FCSTD DOCUMENT  (FreeCAD 0.22R37100 (Git))
Label: composit_stand8_model
License: All rights reserved
LicenseURL: http://en.wikipedia.org/wiki/All_rights_reserved
objects: App::Link×25, App::DocumentObjectGroup×4, Part::FeaturePython×2, PartDesign::CoordinateSystem×1, App::FeaturePython×1, PartDesign::Plane×1, App::AnnotationLabel×1, App::Part×1
note: 4 computed .brp shape members not serialized (recipe doc carries the construction recipe); baked Part::Feature solids carry a one-line shape summary decoded from their .brp
EXTERNAL_REF file=composit_stand8.FCStd obj=Local_CS005
EXTERNAL_REF file=composit_stand8.FCStd obj=Body
EXTERNAL_REF file=composit_stand8.FCStd obj=Local_CS004
EXTERNAL_REF file=composit_stand8.FCStd obj=Local_CS006
EXTERNAL_REF file=composit_stand8.FCStd obj=Body003
EXTERNAL_REF file=composit_stand8.FCStd obj=Local_CS007
EXTERNAL_REF file=composit_stand8.FCStd obj=Local_CS008
EXTERNAL_REF file=composit_stand8.FCStd obj=Local_CS010
EXTERNAL_REF file=composit_stand8.FCStd obj=Body002
EXTERNAL_REF file=composit_stand8.FCStd obj=Local_CS011
EXTERNAL_REF file=composit_stand8.FCStd obj=Local_CS012
EXTERNAL_REF file=composit_stand8.FCStd obj=Local_CS013
EXTERNAL_REF file=composit_stand8.FCStd obj=Body004
EXTERNAL_REF file=composit_stand8.FCStd obj=Local_CS015
EXTERNAL_REF file=composit_stand8.FCStd obj=Local_CS016
EXTERNAL_REF file=composit_stand8.FCStd obj=Body005
EXTERNAL_REF file=composit_stand8.FCStd obj=Local_CS017
EXTERNAL_REF file=composit_stand8.FCStd obj=Body006
EXTERNAL_REF file=composit_stand8.FCStd obj=Local_CS014
EXTERNAL_REF file=composit_stand8.FCStd obj=Local_CS018
EXTERNAL_REF file=composit_stand8.FCStd obj=Local_CS019
EXTERNAL_REF file=composit_stand8.FCStd obj=Part
EXTERNAL_REF file=composit_stand8.FCStd obj=Local_CS020
EXTERNAL_REF file=composit_stand8.FCStd obj=Body007
EXTERNAL_REF file=composit_stand8.FCStd obj=Local_CS025
EXTERNAL_REF file=composit_stand8.FCStd obj=Local_CS026
EXTERNAL_REF file=composit_stand8.FCStd obj=Body012
EXTERNAL_REF file=composit_stand8.FCStd obj=Local_CS027
EXTERNAL_REF file=composit_stand8.FCStd obj=Body013
EXTERNAL_REF file=ULZ-P02-14W.FCStd obj=Local_CS
EXTERNAL_REF file=composit_stand8.FCStd obj=Local_CS028
EXTERNAL_REF file=ULZ-P02-14W.FCStd obj=Body
EXTERNAL_REF file=composit_stand8.FCStd obj=Local_CS030
EXTERNAL_REF file=composit_stand8.FCStd obj=Local_CS032
EXTERNAL_REF file=composit_stand8.FCStd obj=Body018
EXTERNAL_REF file=composit_stand8.FCStd obj=Local_CS031
EXTERNAL_REF file=composit_stand8.FCStd obj=Body019
EXTERNAL_REF file=composit_stand8.FCStd obj=Local_CS033
EXTERNAL_REF file=composit_stand8.FCStd obj=Body017
EXTERNAL_REF file=composit_electric_shield.FCStd obj=Local_CS
EXTERNAL_REF file=composit_stand8.FCStd obj=Local_CS034
EXTERNAL_REF file=composit_electric_shield.FCStd obj=Body
EXTERNAL_REF file=composit_stand8.FCStd obj=Local_CS037
EXTERNAL_REF file=composit_stand8.FCStd obj=Body026
EXTERNAL_REF file=composit_stand8.FCStd obj=Local_CS038
EXTERNAL_REF file=composit_stand8.FCStd obj=Local_CS039
EXTERNAL_REF file=composit_stand8.FCStd obj=Body027
EXTERNAL_REF file=composit_stand8.FCStd obj=Local_CS040
EXTERNAL_REF file=composit_stand8.FCStd obj=Local_CS041
EXTERNAL_REF file=composit_stand8.FCStd obj=Body030

FEATURE [App::DocumentObjectGroup] Parts
FEATURE [PartDesign::CoordinateSystem] LCS_Origin
  AttacherType = Attacher::AttachEngine3D
  AttachmentSupport = -> [XY_Plane]
  MapMode = 2
FEATURE [App::DocumentObjectGroup] Constraints
FEATURE [App::FeaturePython] Variables  # WARN: FeaturePython — macro-defined, semantics opaque (R4)
  Type = App::PropertyContainer
FEATURE [App::DocumentObjectGroup] Configurations
FEATURE [App::Link] face
  AttachedBy = #Local_CS005
  AttachedTo = Parent Assembly#LCS_Origin
  AttachmentOffset = pos=(0,0,0) rot=(0,0,1;3.14159rad)
  LinkPlacement = pos=(0,0,0) rot=(0,0,1;3.14159rad)
  LinkedObject = -> <external composit_stand8.FCStd>#Body
  Placement = pos=(0,0,0) rot=(0,0,1;3.14159rad)
  SolverId = Asm4EE
  expr: Placement = LCS_Origin.Placement * AttachmentOffset * composit_stand8#Local_CS005.Placement ^ -1
FEATURE [App::Link] sink
  AttachedBy = #Local_CS004
  AttachedTo = face#Local_CS006
  LinkPlacement = pos=(-319.563,-20,100) rot=(0,0,1;3.14159rad)
  LinkedObject = -> <external composit_stand8.FCStd>#Body003
  Placement = pos=(-319.563,-20,100) rot=(0,0,1;3.14159rad)
  SolverId = Asm4EE
  expr: Placement = face.Placement * composit_stand8#Local_CS006.Placement * AttachmentOffset * composit_stand8#Local_CS004.Placement ^ -1
FEATURE [App::Link] sink001
  AttachedBy = #Local_CS004
  AttachedTo = face#Local_CS007
  LinkPlacement = pos=(319.563,-20,100) rot=(0,0,1;3.14159rad)
  LinkedObject = -> <external composit_stand8.FCStd>#Body003
  Placement = pos=(319.563,-20,100) rot=(0,0,1;3.14159rad)
  SolverId = Asm4EE
  expr: Placement = face.Placement * composit_stand8#Local_CS007.Placement * AttachmentOffset * composit_stand8#Local_CS004.Placement ^ -1
FEATURE [App::Link] dropper_fix_composit
  AttachedBy = #Local_CS008
  AttachedTo = face#Local_CS010
  AttachmentOffset = pos=(0,0,0.4) rot=(0,0,1;0rad)
  LinkPlacement = pos=(-319.563,3.91e-14,1100.4) rot=(0,0,1;3.14159rad)
  LinkedObject = -> <external composit_stand8.FCStd>#Body002
  Placement = pos=(-319.563,3.91e-14,1100.4) rot=(0,0,1;3.14159rad)
  SolverId = Asm4EE
  expr: Placement = face.Placement * composit_stand8#Local_CS010.Placement * AttachmentOffset * composit_stand8#Local_CS008.Placement ^ -1
FEATURE [App::Link] dropper_fix_composit001
  AttachedBy = #Local_CS008
  AttachedTo = face#Local_CS011
  AttachmentOffset = pos=(0,0,0.4) rot=(0,0,1;0rad)
  LinkPlacement = pos=(319.563,-3.91e-14,1100.4) rot=(0,0,1;3.14159rad)
  LinkedObject = -> <external composit_stand8.FCStd>#Body002
  Placement = pos=(319.563,-3.91e-14,1100.4) rot=(0,0,1;3.14159rad)
  SolverId = Asm4EE
  expr: Placement = face.Placement * composit_stand8#Local_CS011.Placement * AttachmentOffset * composit_stand8#Local_CS008.Placement ^ -1
FEATURE [App::Link] dropper_fix_PP
  AttachedBy = #Local_CS012
  AttachedTo = dropper_fix_composit#Local_CS013
  LinkPlacement = pos=(-319.563,3.91e-14,1103.4) rot=(0,0,1;3.14159rad)
  LinkedObject = -> <external composit_stand8.FCStd>#Body004
  Placement = pos=(-319.563,3.91e-14,1103.4) rot=(0,0,1;3.14159rad)
  SolverId = Asm4EE
  expr: Placement = dropper_fix_composit.Placement * composit_stand8#Local_CS013.Placement * AttachmentOffset * composit_stand8#Local_CS012.Placement ^ -1
FEATURE [App::Link] dropper_fix_PP001
  AttachedBy = #Local_CS012
  AttachedTo = dropper_fix_composit001#Local_CS013
  LinkPlacement = pos=(319.563,-3.91e-14,1103.4) rot=(0,0,1;3.14159rad)
  LinkedObject = -> <external composit_stand8.FCStd>#Body004
  Placement = pos=(319.563,-3.91e-14,1103.4) rot=(0,0,1;3.14159rad)
  SolverId = Asm4EE
  expr: Placement = dropper_fix_composit001.Placement * composit_stand8#Local_CS013.Placement * AttachmentOffset * composit_stand8#Local_CS012.Placement ^ -1
FEATURE [App::Link] bar001
  AttachedBy = #Local_CS016
  AttachedTo = face#Local_CS015
  LinkPlacement = pos=(636.126,-17,883.5) rot=(0,1,0;4.71239rad)
  LinkedObject = -> <external composit_stand8.FCStd>#Body005
  Placement = pos=(636.126,-17,883.5) rot=(0,1,0;4.71239rad)
  SolverId = Asm4EE
  expr: Placement = face.Placement * composit_stand8#Local_CS015.Placement * AttachmentOffset * composit_stand8#Local_CS016.Placement ^ -1
FEATURE [App::Link] bar_fix001
  AttachedBy = #Local_CS017
  AttachedTo = bar001#Local_CS016
  AttachmentOffset = pos=(0,16,0) rot=(0,0,1;0rad)
  LinkPlacement = pos=(636.126,-1,883.5) rot=(-0.707107,0,0.707107;3.14159rad)
  LinkedObject = -> <external composit_stand8.FCStd>#Body006
  Placement = pos=(636.126,-1,883.5) rot=(-0.707107,0,0.707107;3.14159rad)
  SolverId = Asm4EE
  expr: Placement = bar001.Placement * composit_stand8#Local_CS016.Placement * AttachmentOffset * composit_stand8#Local_CS017.Placement ^ -1
FEATURE [App::Link] bar002
  AttachedBy = #Local_CS016
  AttachedTo = face#Local_CS014
  LinkPlacement = pos=(636.126,-17,220) rot=(0,1,0;4.71239rad)
  LinkedObject = -> <external composit_stand8.FCStd>#Body005
  Placement = pos=(636.126,-17,220) rot=(0,1,0;4.71239rad)
  SolverId = Asm4EE
  expr: Placement = face.Placement * composit_stand8#Local_CS014.Placement * AttachmentOffset * composit_stand8#Local_CS016.Placement ^ -1
FEATURE [App::Link] bar_fix
  AttachedBy = #Local_CS017
  AttachedTo = bar002#Local_CS016
  LinkPlacement = pos=(636.126,-17,220) rot=(-0.707107,0,0.707107;3.14159rad)
  LinkedObject = -> <external composit_stand8.FCStd>#Body006
  Placement = pos=(636.126,-17,220) rot=(-0.707107,0,0.707107;3.14159rad)
  SolverId = Asm4EE
  expr: Placement = bar002.Placement * composit_stand8#Local_CS016.Placement * AttachmentOffset * composit_stand8#Local_CS017.Placement ^ -1
FEATURE [App::Link] bar_fix002
  AttachedBy = #Local_CS017
  AttachedTo = bar001#Local_CS018
  LinkPlacement = pos=(-636.126,-17,883.5) rot=(-0.707107,0,-0.707107;3.14159rad)
  LinkedObject = -> <external composit_stand8.FCStd>#Body006
  Placement = pos=(-636.126,-17,883.5) rot=(-0.707107,0,-0.707107;3.14159rad)
  SolverId = Asm4EE
  expr: Placement = bar001.Placement * composit_stand8#Local_CS018.Placement * AttachmentOffset * composit_stand8#Local_CS017.Placement ^ -1
FEATURE [App::Link] bar_fix003
  AttachedBy = #Local_CS017
  AttachedTo = bar002#Local_CS018
  LinkPlacement = pos=(-636.126,-17,220) rot=(-0.707107,0,-0.707107;3.14159rad)
  LinkedObject = -> <external composit_stand8.FCStd>#Body006
  Placement = pos=(-636.126,-17,220) rot=(-0.707107,0,-0.707107;3.14159rad)
  SolverId = Asm4EE
  expr: Placement = bar002.Placement * composit_stand8#Local_CS018.Placement * AttachmentOffset * composit_stand8#Local_CS017.Placement ^ -1
FEATURE [App::Link] modules
  AttachedBy = #Local_CS019
  AttachedTo = face#Local_CS005
  LinkPlacement = pos=(0,0,0) rot=(0,0,1;3.14159rad)
  LinkedObject = -> <external composit_stand8.FCStd>#Part
  Placement = pos=(0,0,0) rot=(0,0,1;3.14159rad)
  SolverId = Asm4EE
  expr: Placement = face.Placement * composit_stand8#Local_CS005.Placement * AttachmentOffset * composit_stand8#Local_CS019.Placement ^ -1
FEATURE [App::Link] sink_back
  AttachedBy = #Local_CS020
  AttachedTo = sink#Local_CS004
  LinkPlacement = pos=(-319.563,-17,100) rot=(0,0,1;3.14159rad)
  LinkedObject = -> <external composit_stand8.FCStd>#Body007
  Placement = pos=(-319.563,-17,100) rot=(0,0,1;3.14159rad)
  SolverId = Asm4EE
  expr: Placement = sink.Placement * composit_stand8#Local_CS004.Placement * AttachmentOffset * composit_stand8#Local_CS020.Placement ^ -1
FEATURE [PartDesign::Plane] Plane_1
  Length = 100
  MapMode = 4
  Placement = pos=(0,0,0) rot=(0.57735,0.57735,0.57735;2.0944rad)
  ResizeMode = 1
  Width = 100
FEATURE [Part::FeaturePython] Mirror_sink_back  # Draft array (typed FeaturePython)
  ArrayType = Mirror Array
  Axis = -> Plane_1
  AxisPlacement = pos=(0,0,0) rot=(0.57735,0.57735,0.57735;2.0944rad)
  Count = 2
  Index = 1
  PlacementList = 2 placements: [(-319.563,-17,100),(319.563,-17,100)]
  Placer = pos=(-34,200,639.126) rot=(0,0,1;3.14159rad)
  ScaleList = (2) [(1,1,1),(-1,-1,-1)]
  Scaler = -1
  ShowElement = false
  SourceObject = -> sink_back
  expr: .Placer.Base = .Placer.Rotation * minvert(.AxisPlacement) * .SourceObject.Placement.Base * -2 * (Index % 2)
  expr: .Placer.Rotation.Angle = 180 * (Index % 2)
  expr: Scaler = 1 - 2 * (Index % 2)
FEATURE [App::Link] lamp_fix
  AttachedBy = #Local_CS026
  AttachedTo = face#Local_CS025
  LinkPlacement = pos=(-319.563,3.91e-14,182) rot=(0,0,1;3.14159rad)
  LinkedObject = -> <external composit_stand8.FCStd>#Body012
  Placement = pos=(-319.563,3.91e-14,182) rot=(0,0,1;3.14159rad)
  SolverId = Asm4EE
  expr: Placement = face.Placement * composit_stand8#Local_CS025.Placement * AttachmentOffset * composit_stand8#Local_CS026.Placement ^ -1
FEATURE [App::Link] lamp_fix_mirror
  AttachedBy = #Local_CS027
  AttachedTo = face#Local_CS025
  LinkPlacement = pos=(-319.563,3.91e-14,182) rot=(0,0,1;3.14159rad)
  LinkedObject = -> <external composit_stand8.FCStd>#Body013
  Placement = pos=(-319.563,3.91e-14,182) rot=(0,0,1;3.14159rad)
  SolverId = Asm4EE
  expr: Placement = face.Placement * composit_stand8#Local_CS025.Placement * AttachmentOffset * composit_stand8#Local_CS027.Placement ^ -1
FEATURE [App::Link] Body
  AttachedBy = #Local_CS
  AttachedTo = lamp_fix#Local_CS028
  LinkPlacement = pos=(-600.201,-195.271,632) rot=(0.313146,0.671543,0.671543;2.53465rad)
  LinkedObject = -> <external ULZ-P02-14W.FCStd>#Body
  Placement = pos=(-600.201,-195.271,632) rot=(0.313146,0.671543,0.671543;2.53465rad)
  SolverId = Asm4EE
  expr: Placement = lamp_fix.Placement * composit_stand8#Local_CS028.Placement * AttachmentOffset * ULZ_P02_14W#Local_CS.Placement ^ -1
FEATURE [App::Link] cap_outer
  AttachedBy = #Local_CS030
  AttachedTo = face#Local_CS032
  LinkPlacement = pos=(0,0,1100) rot=(0,0,1;3.14159rad)
  LinkedObject = -> <external composit_stand8.FCStd>#Body018
  Placement = pos=(0,0,1100) rot=(0,0,1;3.14159rad)
  SolverId = Asm4EE
  expr: Placement = face.Placement * composit_stand8#Local_CS032.Placement * AttachmentOffset * composit_stand8#Local_CS030.Placement ^ -1
FEATURE [App::Link] cap_inner
  AttachedBy = #Local_CS031
  AttachedTo = cap_outer#Local_CS030
  LinkPlacement = pos=(0,0,1100) rot=(0,0,1;3.14159rad)
  LinkedObject = -> <external composit_stand8.FCStd>#Body019
  Placement = pos=(0,0,1100) rot=(0,0,1;3.14159rad)
  SolverId = Asm4EE
  expr: Placement = cap_outer.Placement * composit_stand8#Local_CS030.Placement * AttachmentOffset * composit_stand8#Local_CS031.Placement ^ -1
FEATURE [App::Link] drain_holder
  AttachedBy = #Local_CS033
  AttachedTo = face#Local_CS005
  LinkPlacement = pos=(0,0,0) rot=(0,0,1;3.14159rad)
  LinkedObject = -> <external composit_stand8.FCStd>#Body017
  Placement = pos=(0,0,0) rot=(0,0,1;3.14159rad)
  SolverId = Asm4EE
  expr: Placement = face.Placement * composit_stand8#Local_CS005.Placement * AttachmentOffset * composit_stand8#Local_CS033.Placement ^ -1
FEATURE [Part::FeaturePython] DistPoints  # WARN: FeaturePython — macro-defined, semantics opaque (R4)
FEATURE [App::AnnotationLabel] MeasureLbl
  BasePosition = (10,-87.9055,26.7108)
  LabelText = D = 34,1891 mm
  TextPosition = (0,0,0)
FEATURE [App::DocumentObjectGroup] Measures
  Group = -> [DistPoints,MeasureLbl]
FEATURE [App::Link] composit_electric_shield_inner
  AttachedBy = #Local_CS
  AttachedTo = face#Local_CS034
  LinkPlacement = pos=(605.726,-60,610) rot=(0.57735,0.57735,0.57735;2.0944rad)
  LinkedObject = -> <external composit_electric_shield.FCStd>#Body
  Placement = pos=(605.726,-60,610) rot=(0.57735,0.57735,0.57735;2.0944rad)
  SolverId = Asm4EE
  expr: Placement = face.Placement * composit_stand8#Local_CS034.Placement * AttachmentOffset * composit_electric_shield#Local_CS.Placement ^ -1
FEATURE [App::Link] basin_shield_wall
  AttachedBy = #Local_CS037
  AttachedTo = face#Local_CS005
  AttachmentOffset = pos=(0,0,-500) rot=(0,0,1;0rad)
  LinkPlacement = pos=(0,0,-500) rot=(0,0,1;3.14159rad)
  LinkedObject = -> <external composit_stand8.FCStd>#Body026
  Placement = pos=(0,0,-500) rot=(0,0,1;3.14159rad)
  SolverId = Asm4EE
  expr: Placement = face.Placement * composit_stand8#Local_CS005.Placement * AttachmentOffset * composit_stand8#Local_CS037.Placement ^ -1
FEATURE [App::Link] basin_shield_top
  AttachedBy = #Local_CS039
  AttachedTo = basin_shield_wall#Local_CS038
  LinkPlacement = pos=(0,0,-252) rot=(0,0,1;3.14159rad)
  LinkedObject = -> <external composit_stand8.FCStd>#Body027
  Placement = pos=(0,0,-252) rot=(0,0,1;3.14159rad)
  SolverId = Asm4EE
  expr: Placement = basin_shield_wall.Placement * composit_stand8#Local_CS038.Placement * AttachmentOffset * composit_stand8#Local_CS039.Placement ^ -1
FEATURE [App::Link] basin_shield_corrugation
  AttachedBy = #Local_CS041
  AttachedTo = basin_shield_top#Local_CS040
  LinkPlacement = pos=(0,0,-252) rot=(0,0,1;3.14159rad)
  LinkedObject = -> <external composit_stand8.FCStd>#Body030
  Placement = pos=(0,0,-252) rot=(0,0,1;3.14159rad)
  SolverId = Asm4EE
  expr: Placement = basin_shield_top.Placement * composit_stand8#Local_CS040.Placement * AttachmentOffset * composit_stand8#Local_CS041.Placement ^ -1
FEATURE [App::Part] Assembly
  AssemblyType = Part::Link
  Group = -> [LCS_Origin,Constraints,Variables,Configurations,face,sink,sink001,dropper_fix_composit,dropper_fix_composit001,dropper_fix_PP,dropper_fix_PP001,bar001,bar_fix001,bar002,bar_fix,bar_fix002,bar_fix003,modules,sink_back,Plane_1,Mirror_sink_back,lamp_fix,lamp_fix_mirror,Body,cap_outer,cap_inner,drain_holder,composit_electric_shield_inner,basin_shield_wall,basin_shield_top,basin_shield_corrugation]
  Origin = -> Origin
  Type = Assembly

RESOLVED EXTERNAL PARTS (link-assembly join: the EXTERNAL_REF files above that resolve inside this repo's crawl, each included once):
---- part ULZ-P02-14W.FCStd = doc fcstd_d946428e1785 ----
FCSTD DOCUMENT  (FreeCAD 1.1R38827 (Git))
Label: ULZ-P02-14W
License: All rights reserved
LicenseURL: http://en.wikipedia.org/wiki/All_rights_reserved
objects: Sketcher::SketchObject×4, Part::FeaturePython×4, App::DocumentObjectGroup×3, Path::FeaturePython×3, App::FeaturePython×1, Part::Part2DObjectPython×1, PartDesign::SubShapeBinder×1, PartDesign::Pad×1, PartDesign::CoordinateSystem×1, PartDesign::Body×1
note: 20 computed .brp shape members not serialized (recipe doc carries the construction recipe); baked Part::Feature solids carry a one-line shape summary decoded from their .brp

FEATURE [Sketcher::SketchObject] Sketch  label="holes"
  ArcFitTolerance = 0
  FullyConstrained = true
  MakeInternals = false
  sketch-geometry (3):
    g0: Circle CenterX=-4.15 CenterY=445 CenterZ=0 NormalX=0 NormalY=0 NormalZ=1 AngleXU=0 Radius=1.6
    g1: Circle CenterX=4.15 CenterY=-445 CenterZ=0 NormalX=0 NormalY=0 NormalZ=1 AngleXU=0 Radius=1.6
    g2: GeomPoint [constr] X=-9.05 Y=0 Z=0
  constraints (8):
    c: Symmetric(g1,g0,g-1)
    c: Distance(g0,g1) = 890.039
    c: PointOnObject(g2,g-1)
    c: DistanceX(g2,g0) = 4.9
    c: DistanceX(g2) = -9.05
    c: DistanceY(g1,g0) = 890
    c: Equal(g1,g0)
    c: Diameter(g1) = 3.2
FEATURE [App::FeaturePython] SetupSheet  # Path/CAM operation (typed FeaturePython)
  ClearanceHeightExpression = OpStockZMax+SetupSheet.ClearanceHeightOffset
  ClearanceHeightOffset = 5
  CoolantMode = 0
  CoolantModes = None | Flood | Mist
  FinalDepthExpression = -0.1 mm
  HorizRapid = 0
  ProfileDirection = 1
  ProfileSide = 0
  ProfileUseComp = true
  ProfileprocessCircles = true
  ProfileprocessHoles = true
  ProfileprocessPerimeter = true
  SafeHeightExpression = OpStockZMax+SetupSheet.SafeHeightOffset
  SafeHeightOffset = 3
  StartDepthExpression = 3 mm
  StepDownExpression = 4 mm
  VertRapid = 0
FEATURE [Part::Part2DObjectPython] Clone2D  label="Model-Sketch"  # Draft 2D object (typed FeaturePython)
  Fuse = false
  Objects = -> [Sketch]
  PathResource = Model
  Placement = pos=(-5.75,446.581,0) rot=(0,0,1;0rad)
  Scale = (1,1,1)
FEATURE [App::DocumentObjectGroup] Model
  Group = -> [Clone2D]
FEATURE [Part::FeaturePython] ToolBit  label="3.175mm Endmill"  # Path/CAM toolbit (typed FeaturePython)
  BitPropertyNames = Chipload | CuttingEdgeHeight | Diameter | Flutes | Length | Material | ShankDiameter | SpindleDirection
  BitShape = <path>
  Chipload = 0
  CuttingEdgeHeight = 30
  Diameter = 3.175
  Flutes = 0
  Length = 10
  Material = 0
  ShankDiameter = 3
  ShapeName = endmill
  SpindleDirection = 0
FEATURE [Path::FeaturePython] __175mm_Endmill  label="3.175mm Endmill001"  # Path/CAM operation (typed FeaturePython)
  HorizFeed = 33.3333
  HorizRapid = 0
  SpindleDir = 0
  SpindleSpeed = 18000
  Tool = -> ToolBit
  ToolNumber = 1
  VertFeed = 8.33333
  VertRapid = 0
  expr: HorizRapid = SetupSheet.HorizRapid
  expr: VertRapid = SetupSheet.VertRapid
FEATURE [App::DocumentObjectGroup] Tools
  Group = -> [__175mm_Endmill]
FEATURE [Part::FeaturePython] Stock  # WARN: FeaturePython — macro-defined, semantics opaque (R4)
  Base = -> Model
  ExtXneg = 1
  ExtXpos = 1
  ExtYneg = 1
  ExtYpos = 1
  ExtZneg = 0
  ExtZpos = 1
  Placement = pos=(-5.89217,-448.284,0) rot=(0,0,1;0rad)
  StockType = FromBase
FEATURE [Path::FeaturePython] Profile  # Path/CAM operation (typed FeaturePython)
  Active = true
  AreaParams:
    Tolerance = 1e-07
    FitArcs = True
    Simplify = False
    CleanDistance = 0.0
    Accuracy = 0.01
    Unit = 1.0
    MinArcPoints = 4
    MaxArcPoints = 100
    ClipperScale = 10000000.0
    Fill = 0
    Coplanar = 0
    Reorient = True
    Outline = False
    Explode = False
    OpenMode = 0
    Deflection = 0.01
    SubjectFill = 0
    ClipFill = 0
    Offset = -1.5875
    ExtraPass = 0
    Stepover = 0.0
    LastStepover = 0.0
    JoinType = 0
    EndType = 0
    MiterLimit = 2.0
    RoundPrecision = 0.0
    PocketMode = 0
    ToolRadius = 1.0
    PocketExtraOffset = 0.0
    PocketStepover = 0.0
    PocketLastStepover = 0.0
    FromCenter = False
    Angle = 45.0
    AngleShift = 0.0
    Shift = 0.0
    Thicken = False
    SectionCount = -1
    Stepdown = 1.0
    SectionOffset = 0.0
    SectionTolerance = 1e-06
    SectionMode = 2
    Project = False
  ClearanceHeight = 6
  CoolantMode = 0
  CycleTime = 00:00:57
  Direction = 1
  FinalDepth = -0.1
  HandleMultipleFeatures = 0
  JoinType = 0
  MiterLimit = 0.1
  OffsetExtra = 0
  OpFinalDepth = 0
  OpStartDepth = 1
  OpStockZMax = 1
  OpStockZMin = 0
  OpToolDiameter = 3.175
  PathParams = {'orientation': 1, 'feedrate': 33.333333333333336, 'feedrate_v': 8.333333333333334, 'verbose': True, 'resume_height': 4.0, 'retraction': 6.0, 'return_end': True, 'preamble': False}
  SafeHeight = 4
  Side = 1
  SplitArcs = false
  StartDepth = 3
  StartPoint = (0,0,0)
  StepDown = 4
  ToolController = -> __175mm_Endmill
  UseComp = true
  UseStartPoint = false
  processCircles = true
  processHoles = true
  processPerimeter = true
  expr: ClearanceHeight = OpStockZMax + SetupSheet.ClearanceHeightOffset
  expr: FinalDepth = -0.1 mm
  expr: SafeHeight = OpStockZMax + SetupSheet.SafeHeightOffset
  expr: StartDepth = 3 mm
  expr: StepDown = 4 mm
FEATURE [App::DocumentObjectGroup] Operations
  Group = -> [Profile]
FEATURE [Path::FeaturePython] Job  # Path/CAM operation (typed FeaturePython)
  CycleTime = 00:00:57
  Fixtures = G54
  GeometryTolerance = 0.01
  JobType = 0
  LastPostProcessDate = 2023-12-11 14:23:56.391449
  LastPostProcessOutput = <userpath>/2CAF-B51C/Job-0.tap
  Model = -> Model
  Operations = -> Operations
  OrderOutputBy = 2
  PostProcessor = 3
  PostProcessorOutputFile = %j.tap
  SetupSheet = -> SetupSheet
  SplitOutput = true
  Stock = -> Stock
  Tools = -> Tools
FEATURE [Part::FeaturePython] BoundBox  label="BoundBox of Model-Sketch"  # WARN: FeaturePython — macro-defined, semantics opaque (R4)
  Center = (-5.75,446.581,0)
  CompoundTraversal = 0
  OrientMode = 0
  Padding = 0
  Precision = false
  ScaleFactor = 1
  ShapeLink = -> Clone2D
  Size = (11.5,893.177,0)
FEATURE [Sketcher::SketchObject] Sketch001
  ArcFitTolerance = 0
  FullyConstrained = true
  MakeInternals = false
  Placement = pos=(0,0,0) rot=(1,0,0;1.5708rad)
  sketch-geometry (7):
    g0: LineSegment StartX=-7.3 StartY=1.25 StartZ=0 EndX=7.3 EndY=1.25 EndZ=0
    g1: GeomPoint [constr] X=0 Y=9.25 Z=0
    g2: ArcOfEllipse CenterX=5.1e-15 CenterY=1.25 CenterZ=0 NormalX=0 NormalY=0 NormalZ=1 MajorRadius=8 MinorRadius=7.3 AngleXU=-1.5708 StartAngle=1.5708 EndAngle=4.71239
    g3: LineSegment [constr] StartX=1e-14 StartY=-6.75 StartZ=0 EndX=0 EndY=9.25 EndZ=0
    g4: LineSegment [constr] StartX=7.3 StartY=1.25 StartZ=0 EndX=-7.3 EndY=1.25 EndZ=0
    g5: GeomPoint [constr] X=7.7e-15 Y=-2.02261 Z=0
    g6: GeomPoint [constr] X=3e-15 Y=4.52261 Z=0
  constraints (9):
    c: DistanceX(g0,g0) = 14.6
    c: PointOnObject(g1,g-2)
    c: InternalAlignment(g3-g6 -> g2) x4
    c: Coincident(g3,g1)
    c: Perpendicular(g2,g0) = 4.71239
    c: Perpendicular(g2,g0) = 1.5708
    c: Horizontal(g0)
    c: DistanceY(g2,g1) = 8
    c: DistanceY(g-1,g2) = 1.25
FEATURE [Sketcher::SketchObject] Sketch002
  ArcFitTolerance = 0
  FullyConstrained = true
  MakeInternals = false
  Placement = pos=(0,0,0) rot=(1,0,0;1.5708rad)
  sketch-geometry (8):
    g0: LineSegment StartX=-9 StartY=-5e-16 StartZ=0 EndX=9 EndY=-5e-16 EndZ=0
    g1: LineSegment [constr] StartX=-9 StartY=-5e-16 StartZ=0 EndX=0 EndY=11 EndZ=0
    g2: LineSegment [constr] StartX=7e-16 StartY=11 StartZ=0 EndX=9 EndY=0 EndZ=0
    g3: ArcOfEllipse CenterX=0 CenterY=0 CenterZ=0 NormalX=0 NormalY=0 NormalZ=1 MajorRadius=11 MinorRadius=9 AngleXU=1.5708 StartAngle=4.71239 EndAngle=7.85398
    g4: LineSegment [constr] StartX=7e-16 StartY=11 StartZ=0 EndX=-7e-16 EndY=-11 EndZ=0
    g5: LineSegment [constr] StartX=-9 StartY=6e-16 StartZ=0 EndX=9 EndY=-6e-16 EndZ=0
    g6: GeomPoint [constr] X=7e-16 Y=6.32456 Z=0
    g7: GeomPoint [constr] X=-4e-16 Y=-6.32456 Z=0
  constraints (12):
    c: DistanceX(g0,g0) = 18
    c: Coincident(g0,g1)
    c: Coincident(g1,g2)
    c: Coincident(g2,g0)
    c: Distance(g1,g0) = 11
    c: InternalAlignment(g4-g7 -> g3) x4
    c: Perpendicular(g3,g0) = 1.5708
    c: Equal(g1,g2)
    c: Horizontal(g0)
    c: Coincident(g3,g0)
    c: Coincident(g4,g1)
    c: Coincident(g3,g-1)
FEATURE [PartDesign::SubShapeBinder] Binder
  BindCopyOnChange = 0
  BindMode = 0
  ClaimChildren = true
  Context = -> Body [Binder.]
  Fuse = false
  MakeFace = true
  OffsetFill = false
  OffsetIntersection = false
  OffsetJoinType = 0
  OffsetOpenResult = false
  PartialLoad = false
  Relative = true
  Support = -> [Sketch001]
  _Version = 2
FEATURE [PartDesign::Pad] Pad
  Direction = (0,1,0)
  Length = 820
  Length2 = 10
  Midplane = true
  Profile = -> Binder
  Suppressed = false
  Type = 0
FEATURE [PartDesign::CoordinateSystem] Local_CS
  AttacherType = Attacher::AttachEngine3D
  AttachmentSupport = -> [XY_Plane]
  MapMode = 5
FEATURE [PartDesign::Body] Body
  AllowCompound = false
  Group = -> [Binder,Pad,Local_CS]
  Origin = -> Origin
  Tip = -> Pad
FEATURE [Sketcher::SketchObject] Sketch003
  ArcFitTolerance = 0
  FullyConstrained = true
  MakeInternals = false
  Placement = pos=(0,416,0) rot=(0,0,1;0rad)
  sketch-geometry (8):
    g0: LineSegment StartX=-9 StartY=29.05 StartZ=0 EndX=-9 EndY=0 EndZ=0
    g1: LineSegment StartX=-9 StartY=0 StartZ=0 EndX=9 EndY=0 EndZ=0
    g2: LineSegment StartX=9 StartY=0 StartZ=0 EndX=9 EndY=21.4 EndZ=0
    g3: LineSegment StartX=9 StartY=21.4 StartZ=0 EndX=0.256748 EndY=32.3031 EndZ=0
    g4: ArcOfCircle CenterX=-3.8 CenterY=29.05 CenterZ=0 NormalX=0 NormalY=0 NormalZ=1 AngleXU=0 Radius=5.2 StartAngle=0.675901 EndAngle=3.14159
    g5: GeomPoint [constr] X=-9 Y=43.8466 Z=0
    g6: LineSegment [constr] StartX=0 StartY=34.25 StartZ=0 EndX=-3.8 EndY=34.25 EndZ=0
    g7: Circle CenterX=-3.8 CenterY=29.05 CenterZ=0 NormalX=0 NormalY=0 NormalZ=1 AngleXU=0 Radius=2
  constraints (20):
    c: Vertical(g0)
    c: Coincident(g0,g1)
    c: PointOnObject(g1,g-1)
    c: Coincident(g1,g2)
    c: Vertical(g2)
    c: Coincident(g2,g3)
    c: Symmetric(g0,g1,g-2)
    c: PointOnObject(g5,g0)
    c: PointOnObject(g5,g3)
    c: Tangent(g0,g4) = -1.5708
    c: Tangent(g3,g4) = -1.5708
    c: PointOnObject(g6,g-2)
    c: Tangent(g6,g4) = -1.5708
    c: Horizontal(g6)
    c: DistanceY(g6) = 34.25
    c: DistanceX(g0,g1) = 18
    c: DistanceY(g2,g2) = 21.4
    c: Radius(g4) = 5.2
    c: Coincident(g7,g4)
    c: Diameter(g7) = 4
FEATURE [Part::FeaturePython] Array  # Draft array (typed FeaturePython)
  Angle = 360
  ArrayType = 1
  Axis = (0,0,1)
  Base = -> Sketch003
  Center = (0,0,0)
  Count = 2
  Fuse = true
  IntervalAxis = (0,0,0)
  IntervalX = (50,0,0)
  IntervalY = (0,50,0)
  IntervalZ = (0,0,50)
  NumberCircles = 3
  NumberPolar = 2
  NumberX = 2
  NumberY = 2
  NumberZ = 1
  RadialDistance = 50
  Symmetry = 1
  TangentialDistance = 25
note: 1 file-system path scrubbed to <path> (originals preserved in the JSON sidecar)
---- part composit_electric_shield.FCStd = doc fcstd_7e5574ddc39a (52053 chars; too large to inline — full recipe in that document) ----
---- part composit_stand8.FCStd = doc fcstd_39c9c78f2357 (379019 chars; too large to inline — full recipe in that document) ----
